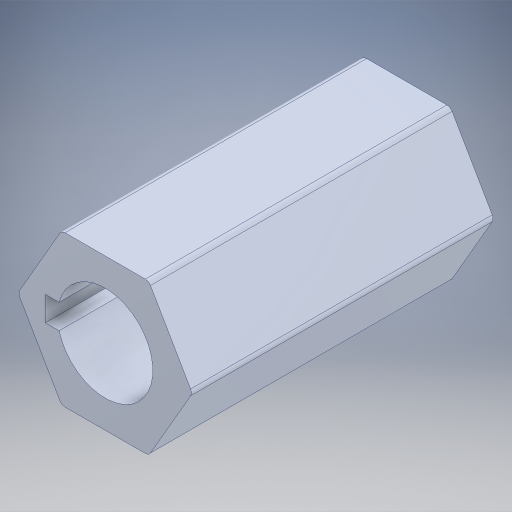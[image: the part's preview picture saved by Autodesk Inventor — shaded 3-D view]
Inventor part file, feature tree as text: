
AUTODESK INVENTOR PART (.ipt)
format: ipt  version: 2024.2 (Build 282272000, 272)  size: 252,416 bytes
history: native  units: in
note: dims shown in document units (in); Inventor stores cm internally (conversion verified against a paired STEP export)
features: fillet x1
ambient origin geometry x8: Origin, YZ Plane, XZ Plane, XY Plane, X Axis, Y Axis, Z Axis, Center Point
bodies: Solid1 (feature_tree)
feature tree (1):
  fillet  "Fillet1"  [1 undecoded]
note: 1 required parameter value undecoded (feature->parameter linkage not recoverable at this tier; creation-order binding heuristic only, values carry confidence <= 0.55)
